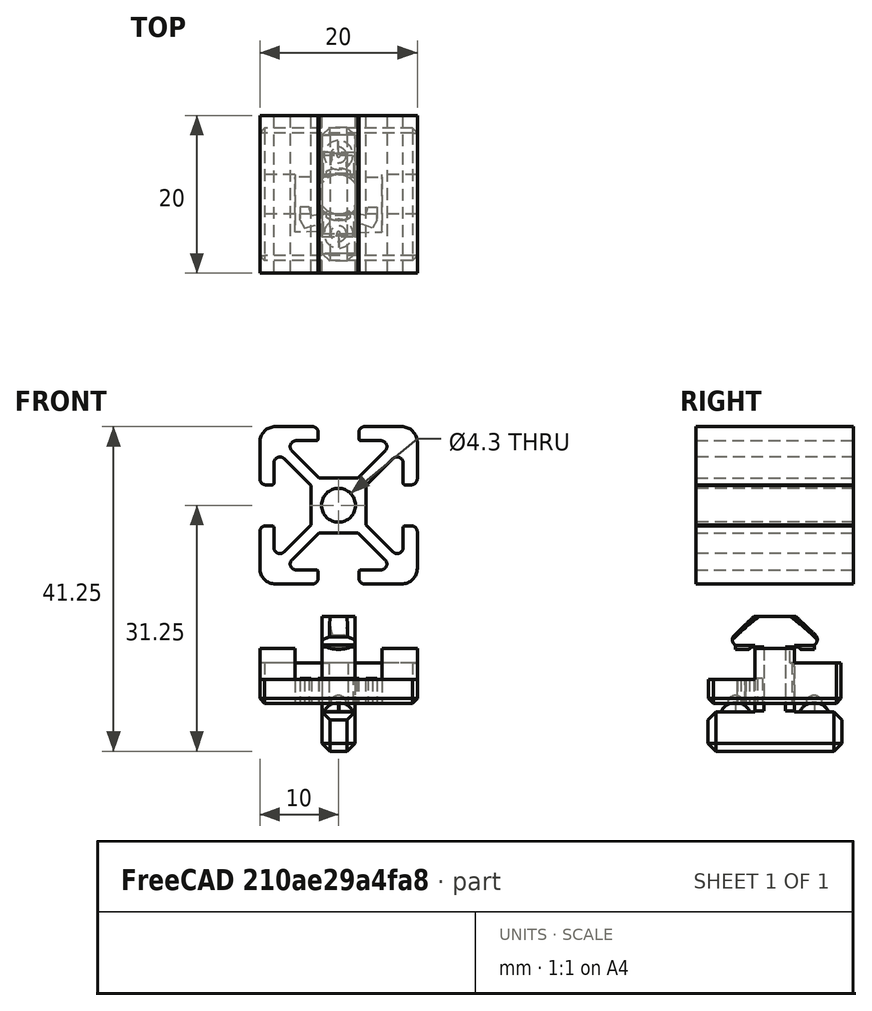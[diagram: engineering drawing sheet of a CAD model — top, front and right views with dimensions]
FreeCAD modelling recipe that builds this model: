
FCSTD DOCUMENT  (FreeCAD 0.18R)
Label: Quickrelease-Parts
License: All rights reserved
LicenseURL: http://en.wikipedia.org/wiki/All_rights_reserved
objects: Sketcher::SketchObject×8, Mesh::Feature×6, PartDesign::Pad×4, PartDesign::Pocket×3, PartDesign::Body×3, PartDesign::PolarPattern×2, PartDesign::Chamfer×2, App::Part×2, PartDesign::SubtractiveSphere×1, PartDesign::Groove×1, PartDesign::AdditiveSphere×1, Part::Compound×1, Spreadsheet::Sheet×1
note: 36 computed .brp shape members not serialized (recipe doc carries the construction recipe); baked Part::Feature solids carry a one-line shape summary decoded from their .brp

FEATURE [Sketcher::SketchObject] Sketch  label="Cutout"
  MapMode = 5
  Support = -> [XY_Plane]
  sketch-geometry (22):
    g0: ArcOfCircle CenterX=0 CenterY=0 CenterZ=0 NormalX=0 NormalY=0 NormalZ=1 AngleXU=0 Radius=2.5 StartAngle=2.64666 EndAngle=3.63653
    g1: ArcOfCircle CenterX=0 CenterY=0 CenterZ=0 NormalX=0 NormalY=0 NormalZ=1 AngleXU=0 Radius=2.5 StartAngle=5.78825 EndAngle=6.77812
    g2: LineSegment StartX=-2.2 StartY=1.18743 StartZ=0 EndX=-2.2 EndY=5.5 EndZ=0
    g3: LineSegment StartX=-2.2 StartY=5.5 StartZ=0 EndX=4.8 EndY=5.5 EndZ=0
    g4: LineSegment StartX=-2.2 StartY=-1.18743 StartZ=0 EndX=-2.2 EndY=-5.5 EndZ=0
    g5: LineSegment StartX=-2.2 StartY=-5.5 StartZ=0 EndX=4.8 EndY=-5.5 EndZ=0
    g6: LineSegment StartX=4.72217 StartY=-2.53995 StartZ=0 EndX=4.8 EndY=-5.5 EndZ=0
    g7: LineSegment StartX=2.2 StartY=-1.18743 StartZ=0 EndX=2.67744 EndY=-3.43203 EndZ=0
    g8: LineSegment StartX=2.67744 StartY=-3.43203 StartZ=0 EndX=1.6 EndY=-3.74347 EndZ=0
    g9: LineSegment StartX=1.6 StartY=-3.74347 StartZ=0 EndX=1.6 EndY=-4.86467 EndZ=0
    g10: LineSegment StartX=1.6 StartY=-4.86467 StartZ=0 EndX=3.24458 EndY=-4.86467 EndZ=0
    g11: LineSegment StartX=3.24458 StartY=-4.86467 StartZ=0 EndX=4.3 EndY=-4.34487 EndZ=0
    g12: LineSegment StartX=4.3 StartY=-4.34487 StartZ=0 EndX=3.77118 EndY=-2.50776 EndZ=0
    g13: LineSegment StartX=2.2 StartY=1.18743 StartZ=0 EndX=2.67744 EndY=3.43203 EndZ=0
    g14: LineSegment StartX=2.67744 StartY=3.43203 StartZ=0 EndX=1.6 EndY=3.74347 EndZ=0
    g15: LineSegment StartX=1.6 StartY=3.74347 StartZ=0 EndX=1.6 EndY=4.86467 EndZ=0
    g16: LineSegment StartX=1.6 StartY=4.86467 StartZ=0 EndX=3.24458 EndY=4.86467 EndZ=0
    g17: LineSegment StartX=3.24458 StartY=4.86467 StartZ=0 EndX=4.3 EndY=4.34487 EndZ=0
    g18: LineSegment StartX=4.3 StartY=4.34487 StartZ=0 EndX=3.65012 EndY=2.51975 EndZ=0
    g19: LineSegment StartX=4.82978 StartY=2.36526 StartZ=0 EndX=4.8 EndY=5.5 EndZ=0
    g20: ArcOfCircle CenterX=4.24748 CenterY=2.5 CenterZ=0 NormalX=0 NormalY=0 NormalZ=1 AngleXU=0 Radius=0.597689 StartAngle=3.10855 EndAngle=6.0558
    g21: ArcOfCircle CenterX=4.24748 CenterY=-2.5 CenterZ=0 NormalX=0 NormalY=0 NormalZ=1 AngleXU=0 Radius=0.476368 StartAngle=6.19922 EndAngle=9.44107
  constraints (48):
    c: Coincident(g0,g1)
    c: Coincident(g0,g-1)
    c: Radius(g0) = 2.5
    c: Coincident(g2,g3)
    c: Coincident(g4,g5)
    c: Coincident(g7,g8)
    c: Coincident(g8,g9)
    c: Coincident(g9,g10)
    c: Coincident(g10,g11)
    c: Coincident(g11,g12)
    c: Coincident(g13,g14)
    c: Coincident(g14,g15)
    c: Coincident(g15,g16)
    c: Coincident(g16,g17)
    c: Coincident(g17,g18)
    c: Coincident(g3,g19)
    c: Coincident(g6,g5)
    c: Coincident(g0,g4)
    c: Coincident(g0,g2)
    c: Coincident(g1,g13)
    c: Coincident(g1,g7)
    c: Vertical(g2)
    c: Horizontal(g3)
    c: Symmetric(g0,g0,g-1)
    c: Vertical(g15)
    c: Symmetric(g13,g7,g-1)
    c: Symmetric(g14,g8,g-1)
    c: Symmetric(g15,g9,g-1)
    c: Horizontal(g16)
    c: Horizontal(g10)
    c: Symmetric(g11,g17,g-1)
    c: Symmetric(g4,g2,g-1)
    c: Coincident(g18,g20)
    c: Coincident(g19,g20)
    c: Coincident(g12,g21)
    c: Coincident(g6,g21)
    c: Symmetric(g20,g21,g-1)
    c: DistanceX(g2,g15) = 3.8
    c: DistanceY(g21,g20) = 5
    c: Symmetric(g5,g3,g-1)
    c: Radius(g1) = 2.5
    c: Vertical(g1,g1)
    c: DistanceX(g0,g1) = 2.2
    c: DistanceY(g4,g2) = 11
    c: DistanceX(g4,g5) = 7
    c: Equal(g16,g10)
    c: DistanceX(g0,g0) = 2.2
    c: DistanceX(g17,g3) = 0.5
FEATURE [Sketcher::SketchObject] Sketch001  label="BodyProfile"
  MapMode = 5
  Placement = pos=(0,0,0) rot=(1,0,0;1.5708rad)
  Support = -> [XZ_Plane]
  expr: Constraints.Clamping Width = Param.thickness + Param.tolerance
  sketch-geometry (9):
    g0: LineSegment StartX=-8.4 StartY=0 StartZ=0 EndX=-8.4 EndY=-5.15 EndZ=0
    g1: LineSegment StartX=-8.4 StartY=-5.15 StartZ=0 EndX=8.4 EndY=-5.15 EndZ=0
    g2: LineSegment StartX=8.4 StartY=-5.15 StartZ=0 EndX=8.4 EndY=-2.15 EndZ=0
    g3: LineSegment StartX=8.4 StartY=-2.15 StartZ=0 EndX=2.5 EndY=-2.15 EndZ=0
    g4: LineSegment StartX=2.5 StartY=-2.15 StartZ=0 EndX=2.5 EndY=0 EndZ=0
    g5: LineSegment StartX=2.5 StartY=0 StartZ=0 EndX=2.5 EndY=1.8 EndZ=0
    g6: LineSegment StartX=2.5 StartY=1.8 StartZ=0 EndX=-2.5 EndY=1.8 EndZ=0
    g7: LineSegment StartX=-2.5 StartY=1.8 StartZ=0 EndX=-2.5 EndY=0 EndZ=0
    g8: LineSegment StartX=-2.5 StartY=0 StartZ=0 EndX=-8.4 EndY=0 EndZ=0
  constraints (25):
    c: Coincident(g2,g3)
    c: Coincident(g3,g4)
    c: Coincident(g4,g5)
    c: Coincident(g5,g6)
    c: Coincident(g6,g7)
    c: Coincident(g7,g8)
    c: Coincident(g0,g8)
    c: Vertical(g0)
    c: Vertical(g2)
    c: Vertical(g4)
    c: Horizontal(g8)
    c: Symmetric(g7,g4,g-2)
    c: Vertical(g5)
    c: Vertical(g7)
    c: DistanceX(g6,g5) = 5
    c: DistanceX(g0,g-1) = 8.4
    c: DistanceY(g7,g6) = 1.8
    c: Horizontal(g6)
    c: Horizontal(g3)
    c: DistanceY(g3,g4) = 2.15  'Clamping Width'
    c: Symmetric(g1,g1,g-2)
    c: PointOnObject(g0,g-1)
    c: DistanceY(g1,g3) = 3
    c: Coincident(g2,g1)
    c: Coincident(g0,g1)
FEATURE [PartDesign::Pad] Pad
  Length = 20
  Length2 = 100
  Midplane = true
  Placement = pos=(0,0,0) rot=(1,0,0;1.5708rad)
  Profile = -> Sketch001
  Type = 0
FEATURE [PartDesign::Pocket] Pocket
  BaseFeature = -> Pad
  Length = 20
  Length2 = 100
  Midplane = true
  Placement = pos=(0,0,0) rot=(1,0,0;1.5708rad)
  Profile = -> Sketch
  Reversed = true
  Type = 0
FEATURE [Sketcher::SketchObject] Sketch009  label="SpringFlat"
  MapMode = 5
  Support = -> [XY_Plane]
  sketch-geometry (4):
    g0: LineSegment StartX=1.17655 StartY=5.27101 StartZ=0 EndX=5.09033 EndY=5.27101 EndZ=0
    g1: LineSegment StartX=5.09033 StartY=5.27101 StartZ=0 EndX=5.09033 EndY=-5.27101 EndZ=0
    g2: LineSegment StartX=5.09033 StartY=-5.27101 StartZ=0 EndX=1.17655 EndY=-5.27101 EndZ=0
    g3: LineSegment StartX=1.17655 StartY=-5.27101 StartZ=0 EndX=1.17655 EndY=5.27101 EndZ=0
  constraints (8):
    c: Coincident(g0,g1)
    c: Coincident(g1,g2)
    c: Coincident(g2,g3)
    c: Coincident(g3,g0)
    c: Horizontal(g0)
    c: Horizontal(g2)
    c: Vertical(g3)
    c: Symmetric(g0,g1,g-1)
FEATURE [PartDesign::Pocket] Pocket001
  BaseFeature = -> Pocket
  Length = 4
  Length2 = 0
  Midplane = true
  Placement = pos=(0,0,0) rot=(1,0,0;1.5708rad)
  Profile = -> Sketch009
  Type = 0
  expr: Length = Param.thickness * 2
FEATURE [PartDesign::SubtractiveSphere] Sphere001
  Angle1 = -90
  Angle2 = 90
  Angle3 = 360
  AttacherType = Attacher::AttachEngine3D
  AttachmentOffset = pos=(5,0,0) rot=(0,0,1;0rad)
  BaseFeature = -> Pocket001
  MapMode = 5
  Placement = pos=(5,-1.1e-15,-5.15) rot=(1,0,0;3.14159rad)
  Radius = 1
  Support = -> [Pocket001]
FEATURE [PartDesign::PolarPattern] PolarPattern002
  Angle = 360
  Axis = -> Z_Axis
  BaseFeature = -> Sphere001
  Occurrences = 2
  Originals = -> [Sphere001]
  Placement = pos=(5,1e-15,-5.15) rot=(1,0,0;3.14159rad)
FEATURE [PartDesign::Chamfer] Chamfer
  Base = -> PolarPattern002 [Edge11,Edge10,Edge9,Edge2,Edge42,Edge36,Edge4,Edge3]
  BaseFeature = -> PolarPattern002
  Placement = pos=(5,1e-15,-5.15) rot=(1,0,0;3.14159rad)
  Size = 0.6
FEATURE [Sketcher::SketchObject] Sketch011
  MapMode = 5
  Support = -> [XY_Plane]
  sketch-geometry (4):
    g0: LineSegment StartX=-2.59862 StartY=-5.51836 StartZ=0 EndX=-1.94057 EndY=-5.51836 EndZ=0
    g1: LineSegment StartX=-1.94057 StartY=-5.51836 StartZ=0 EndX=-1.94057 EndY=5.51836 EndZ=0
    g2: LineSegment StartX=-1.94057 StartY=5.51836 StartZ=0 EndX=-2.59862 EndY=5.51836 EndZ=0
    g3: LineSegment StartX=-2.59862 StartY=5.51836 StartZ=0 EndX=-2.59862 EndY=-5.51836 EndZ=0
  constraints (8):
    c: Coincident(g0,g1)
    c: Coincident(g1,g2)
    c: Coincident(g2,g3)
    c: Coincident(g3,g0)
    c: Horizontal(g0)
    c: Horizontal(g2)
    c: Vertical(g1)
    c: Symmetric(g0,g2,g-1)
FEATURE [PartDesign::Pocket] Pocket002
  BaseFeature = -> Chamfer
  Length = 5
  Length2 = 100
  Placement = pos=(5,1e-15,-5.15) rot=(1,0,0;3.14159rad)
  Profile = -> Sketch011
  Reversed = true
  Type = 0
FEATURE [PartDesign::Body] Body  label="LockBody"
  Group = -> [Sketch,Sketch001,Pad,Pocket,Sketch009,Pocket001,Sphere001,PolarPattern002,Chamfer,Sketch011,Pocket002]
  Origin = -> Origin
  Placement = pos=(0,0,-10) rot=(0,0,-1;1.5708rad)
  Tip = -> Pocket002
FEATURE [Sketcher::SketchObject] Sketch018  label="LockKey-Profile003"
  MapMode = 5
  Placement = pos=(0,0,0) rot=(1,0,0;1.5708rad)
  Support = -> [XZ_Plane010]
  expr: Constraints[23] = Param.thickness + 4.0999999999999996 + Param.tolerance
  sketch-geometry (14):
    g0: LineSegment StartX=-2.5 StartY=2.2 StartZ=0 EndX=-4.9399 EndY=2.2 EndZ=0
    g1: LineSegment StartX=-5.19157 StartY=3.4796 StartZ=0 EndX=-2.66572 EndY=5.8764 EndZ=0
    g2: LineSegment StartX=-2.66572 StartY=5.8764 StartZ=0 EndX=2.66572 EndY=5.8764 EndZ=0
    g3: LineSegment StartX=2.66572 StartY=5.8764 StartZ=0 EndX=5.31297 EndY=3.29057 EndZ=0
    g4: LineSegment StartX=-2.5 StartY=2.2 StartZ=0 EndX=-2.5 EndY=-6.25 EndZ=0
    g5: LineSegment StartX=-2.5 StartY=-6.25 StartZ=0 EndX=-8.5 EndY=-6.25 EndZ=0
    g6: LineSegment StartX=-8.5 StartY=-6.25 StartZ=0 EndX=-8.5 EndY=-11.25 EndZ=0
    g7: LineSegment StartX=-8.5 StartY=-11.25 StartZ=0 EndX=8.5 EndY=-11.25 EndZ=0
    g8: LineSegment StartX=8.5 StartY=-11.25 StartZ=0 EndX=8.5 EndY=-6.25 EndZ=0
    g9: LineSegment StartX=8.5 StartY=-6.25 StartZ=0 EndX=2.5 EndY=-6.25 EndZ=0
    g10: LineSegment StartX=2.5 StartY=-6.25 StartZ=0 EndX=2.5 EndY=2.2 EndZ=0
    g11: LineSegment StartX=2.5 StartY=2.2 StartZ=0 EndX=4.9399 EndY=2.2 EndZ=0
    g12: ArcOfCircle CenterX=-4.55856 CenterY=2.93955 CenterZ=0 NormalX=0 NormalY=0 NormalZ=1 AngleXU=0 Radius=0.832074 StartAngle=2.43527 EndAngle=4.23632
    g13: ArcOfCircle CenterX=4.55856 CenterY=2.93955 CenterZ=0 NormalX=0 NormalY=0 NormalZ=1 AngleXU=0 Radius=0.832074 StartAngle=5.18846 EndAngle=6.71868
  constraints (33):
    c: Coincident(g1,g2)
    c: Coincident(g2,g3)
    c: Coincident(g4,g5)
    c: Coincident(g9,g10)
    c: Coincident(g10,g11)
    c: Horizontal(g0)
    c: Horizontal(g11)
    c: Horizontal(g9)
    c: Horizontal(g5)
    c: Vertical(g6)
    c: Vertical(g8)
    c: Coincident(g13,g3)
    c: Coincident(g13,g11)
    c: Coincident(g12,g1)
    c: Coincident(g12,g0)
    c: Symmetric(g13,g12,g-2)
    c: Equal(g13,g12)
    c: Symmetric(g1,g2,g-2)
    c: Coincident(g0,g4)
    c: Symmetric(g0,g10,g-2)
    c: DistanceX(g0,g10) = 5
    c: Vertical(g4)
    c: Symmetric(g7,g7,g-2)
    c: DistanceY(g4,g-1) = 6.25
    c: DistanceY(g-1,g0) = 2.2
    c: DistanceX(g6,g8) = 17
    c: Equal(g5,g9)
    c: DistanceY(g7,g9) = 5
    c: Coincident(g6,g7)
    c: Coincident(g7,g8)
    c: Coincident(g6,g5)
    c: Coincident(g9,g8)
    c: Equal(g4,g10)
FEATURE [PartDesign::Pad] Pad009
  Length = 4.2
  Length2 = 100
  Midplane = true
  Placement = pos=(0,0,0) rot=(1,0,0;1.5708rad)
  Profile = -> Sketch018
  Type = 0
FEATURE [Sketcher::SketchObject] Sketch019  label="ISP5-Shape003"
  MapMode = 5
  Placement = pos=(0,0,0) rot=(1,0,0;1.5708rad)
  expr: Constraints[29] = 4 + Param.thickness + Param.tolerance
  sketch-geometry (11):
    g0: LineSegment StartX=0 StartY=6.35 StartZ=0 EndX=2.4 EndY=6.35 EndZ=0
    g1: LineSegment StartX=2.4 StartY=6.35 StartZ=0 EndX=5.75 EndY=2.96706 EndZ=0
    g2: LineSegment StartX=5.75 StartY=2.96706 StartZ=0 EndX=5.75 EndY=1.6 EndZ=0
    g3: LineSegment StartX=5.75 StartY=1.6 StartZ=0 EndX=3.3 EndY=1.6 EndZ=0
    g4: LineSegment StartX=2.5 StartY=2 StartZ=0 EndX=2.5 EndY=-6.15 EndZ=0
    g5: LineSegment StartX=2.5 StartY=-6.15 StartZ=0 EndX=6.85109 EndY=-6.15 EndZ=0
    g6: LineSegment StartX=6.85109 StartY=-6.15 StartZ=0 EndX=6.85109 EndY=7.66399 EndZ=0
    g7: LineSegment StartX=6.85109 StartY=7.66399 StartZ=0 EndX=0 EndY=7.66399 EndZ=0
    g8: LineSegment StartX=0 StartY=7.66399 StartZ=0 EndX=0 EndY=6.35 EndZ=0
    g9: LineSegment StartX=2.5 StartY=2 StartZ=0 EndX=3.3 EndY=2 EndZ=0
    g10: LineSegment StartX=3.3 StartY=2 StartZ=0 EndX=3.3 EndY=1.6 EndZ=0
  constraints (30):
    c: Coincident(g0,g1)
    c: Coincident(g1,g2)
    c: Coincident(g2,g3)
    c: Coincident(g4,g5)
    c: Vertical(g4)
    c: Horizontal(g0)
    c: Horizontal(g5)
    c: Horizontal(g3)
    c: Coincident(g7,g8)
    c: Coincident(g8,g0)
    c: Coincident(g6,g7)
    c: Coincident(g5,g6)
    c: Vertical(g6)
    c: Horizontal(g7)
    c: Vertical(g8)
    c: PointOnObject(g0,g-2)
    c: DistanceY(g-1,g3) = 1.6
    c: DistanceX(g-1,g2) = 5.75
    c: Vertical(g2)
    c: DistanceY(g-1,g0) = 6.35
    c: DistanceX(g0,g0) = 2.4
    c: Coincident(g9,g10)
    c: Coincident(g10,g3)
    c: Coincident(g4,g9)
    c: Horizontal(g9)
    c: Vertical(g10)
    c: DistanceY(g-1,g4) = 2
    c: DistanceX(g-1,g4) = 2.5
    c: DistanceX(g9,g9) = 0.8
    c: DistanceY(g4,g-1) = 6.15
FEATURE [Sketcher::SketchObject] Sketch020
  MapMode = 5
  Placement = pos=(0,0,0) rot=(0.57735,0.57735,0.57735;2.0944rad)
  Support = -> [YZ_Plane010]
  sketch-geometry (3):
    g0: ArcOfCircle CenterX=-2e-16 CenterY=5.7 CenterZ=0 NormalX=0 NormalY=0 NormalZ=1 AngleXU=0 Radius=4 StartAngle=4.15967 EndAngle=5.2651
    g1: LineSegment [constr] StartX=0 StartY=0 StartZ=0 EndX=0 EndY=1.7 EndZ=0
    g2: LineSegment StartX=-2.1 StartY=2.29559 StartZ=0 EndX=2.1 EndY=2.29559 EndZ=0
  constraints (9):
    c: Symmetric(g0,g0,g-2)
    c: DistanceX(g0,g0) = 4.2
    c: PointOnObject(g1,g0)
    c: Vertical(g1)
    c: Coincident(g-1,g1)
    c: DistanceY(g1,g1) = 1.7
    c: Radius(g0) = 4
    c: Coincident(g2,g0)
    c: Coincident(g2,g0)
FEATURE [PartDesign::Pad] Pad010
  BaseFeature = -> Pad009
  Length = 10
  Length2 = 100
  Midplane = true
  Placement = pos=(0,0,0) rot=(1,0,0;1.5708rad)
  Profile = -> Sketch020
  Type = 0
FEATURE [PartDesign::Groove] Groove003
  Angle = 360
  Axis = (0,2e-16,1)
  Base = (0,0,0)
  BaseFeature = -> Pad010
  Placement = pos=(0,0,0) rot=(1,0,0;1.5708rad)
  Profile = -> Sketch019
  ReferenceAxis = -> Sketch019 [V_Axis]
FEATURE [PartDesign::AdditiveSphere] Sphere004
  Angle1 = -83
  Angle2 = 90
  Angle3 = 358
  AttacherType = Attacher::AttachEngine3D
  AttachmentOffset = pos=(5,0,-4.2) rot=(0,0,-1;0.017453rad)
  BaseFeature = -> Groove003
  MapMode = 5
  Placement = pos=(5,-1.6e-15,-7.05) rot=(0.999962,0.008727,0;3.14159rad)
  Radius = 2
  Support = -> [Groove003]
FEATURE [PartDesign::PolarPattern] PolarPattern005
  Angle = 360
  Axis = -> Z_Axis010
  BaseFeature = -> Sphere004
  Occurrences = 2
  Originals = -> [Sphere004]
  Placement = pos=(5,2e-15,-7.05) rot=(0.999962,0.008727,0;3.14159rad)
FEATURE [PartDesign::Chamfer] Chamfer004
  Base = -> PolarPattern005 [Face11,Face10,Face12]
  BaseFeature = -> PolarPattern005
  Placement = pos=(5,2e-15,-7.05) rot=(0.999962,0.008727,0;3.14159rad)
  Size = 1
FEATURE [PartDesign::Body] Body007  label="LockKey"
  Group = -> [Pad009,Pad010,Sketch018,Sketch019,Groove003,Sphere004,Sketch020,PolarPattern005,Chamfer004]
  Origin = -> Origin010
  Placement = pos=(0,0,-10) rot=(0,0,-1;1.5708rad)
  Tip = -> Chamfer004
FEATURE [Part::Compound] Compound  label="Key-Body-Combo"
  Links = -> [Body,Body007]
FEATURE [Spreadsheet::Sheet] Spreadsheet  label="Param"
  cells = A1=Sheet Thickness; B1(thickness)=2; C1=The specified thickness of the sheet to clamp.; A2=Sheet Thickness Tolerance; B2(tolerance)=0.14999999999999999; C2=Adds to the sheet thickness and results in the distance between the surface of the extrusion profile and the bottom side of the clamp.
FEATURE [App::Part] Part  label="Key-Clamp-Combo"
  Group = -> [Body,Body007,Compound,Spreadsheet]
  Origin = -> Origin011
FEATURE [Mesh::Feature] Mesh007  label="LockBody-4mm (Meshed)"
  Placement = pos=(0,18,-33) rot=(0,0,1;0rad)
FEATURE [Mesh::Feature] Mesh008  label="LockKey-4mm (Meshed)"
  Placement = pos=(-7.8e-15,57,-3) rot=(0,1,0;1.5708rad)
FEATURE [Mesh::Feature] Mesh009  label="LockKey-3mm (Meshed)001"
  Placement = pos=(-32,0,-7.1e-15) rot=(0,1,0;1.5708rad)
FEATURE [Mesh::Feature] Mesh010  label="LockBody-3mm (Meshed)"
FEATURE [Mesh::Feature] Mesh  label="LockKey-2mm (Meshed)"
  Placement = pos=(0,48,0) rot=(0,1,0;1.5708rad)
FEATURE [Mesh::Feature] Mesh011  label="LockBody-2mm (Meshed)"
FEATURE [App::Part] Part001  label="MeshedParts"
  Group = -> [Mesh007,Mesh008,Mesh009,Mesh010,Mesh,Mesh011]
  Origin = -> Origin012
FEATURE [Sketcher::SketchObject] CopySketch030  label="ISP5-L20-Profile001"
  MapMode = 5
  sketch-geometry (70):
    g0: LineSegment StartX=-2.5 StartY=3.5 StartZ=0 EndX=-5.91967 EndY=6.91967 EndZ=0
    g1: LineSegment StartX=-5.38934 StartY=8.2 StartZ=0 EndX=-2.85 EndY=8.2 EndZ=0
    g2: LineSegment StartX=-3.35 StartY=10 StartZ=0 EndX=-8 EndY=10 EndZ=0
    g3: LineSegment StartX=-10 StartY=8 StartZ=0 EndX=-10 EndY=3.35 EndZ=0
    g4: LineSegment StartX=-9.25 StartY=2.6 StartZ=0 EndX=-8.45 EndY=2.6 EndZ=0
    g5: LineSegment StartX=-8.2 StartY=2.85 StartZ=0 EndX=-8.2 EndY=5.38934 EndZ=0
    g6: LineSegment StartX=-6.91967 StartY=5.91967 StartZ=0 EndX=-3.5 EndY=2.5 EndZ=0
    g7: LineSegment StartX=-2.6 StartY=9.25 StartZ=0 EndX=-2.6 EndY=8.45 EndZ=0
    g8: ArcOfCircle CenterX=-8 CenterY=8 CenterZ=0 NormalX=0 NormalY=0 NormalZ=1 AngleXU=0 Radius=2 StartAngle=1.5708 EndAngle=3.14159
    g9: ArcOfCircle CenterX=-3.35 CenterY=9.25 CenterZ=0 NormalX=0 NormalY=0 NormalZ=1 AngleXU=0 Radius=0.75 StartAngle=6e-16 EndAngle=1.5708
    g10: ArcOfCircle CenterX=-9.25 CenterY=3.35 CenterZ=0 NormalX=0 NormalY=0 NormalZ=1 AngleXU=0 Radius=0.75 StartAngle=3.14159 EndAngle=4.71239
    g11: ArcOfCircle CenterX=-5.38934 CenterY=7.45 CenterZ=0 NormalX=0 NormalY=0 NormalZ=1 AngleXU=0 Radius=0.75 StartAngle=1.5708 EndAngle=3.92699
    g12: ArcOfCircle CenterX=-7.45 CenterY=5.38934 CenterZ=0 NormalX=0 NormalY=0 NormalZ=1 AngleXU=0 Radius=0.75 StartAngle=0.785398 EndAngle=3.14159
    g13: LineSegment [constr] StartX=-5.38934 StartY=7.45 StartZ=0 EndX=-7.45 EndY=5.38934 EndZ=0
    g14: ArcOfCircle CenterX=-2.85 CenterY=8.45 CenterZ=0 NormalX=0 NormalY=0 NormalZ=1 AngleXU=0 Radius=0.25 StartAngle=4.71239 EndAngle=6.28319
    g15: Circle CenterX=0 CenterY=0 CenterZ=0 NormalX=0 NormalY=0 NormalZ=1 AngleXU=0 Radius=2.15
    g16: LineSegment StartX=2.5 StartY=3.5 StartZ=0 EndX=5.91967 EndY=6.91967 EndZ=0
    g17: LineSegment StartX=3.5 StartY=-2.5 StartZ=0 EndX=6.91967 EndY=-5.91967 EndZ=0
    g18: LineSegment StartX=2.5 StartY=-3.5 StartZ=0 EndX=5.91967 EndY=-6.91967 EndZ=0
    g19: LineSegment StartX=-2.5 StartY=-3.5 StartZ=0 EndX=-5.91967 EndY=-6.91967 EndZ=0
    g20: LineSegment StartX=-3.5 StartY=-2.5 StartZ=0 EndX=-6.91967 EndY=-5.91967 EndZ=0
    g21: LineSegment StartX=3.5 StartY=2.5 StartZ=0 EndX=6.91967 EndY=5.91967 EndZ=0
    g22: ArcOfCircle CenterX=-7.45 CenterY=-5.38934 CenterZ=0 NormalX=0 NormalY=0 NormalZ=1 AngleXU=0 Radius=0.75 StartAngle=3.14159 EndAngle=5.49779
    g23: ArcOfCircle CenterX=-5.38934 CenterY=-7.45 CenterZ=0 NormalX=0 NormalY=0 NormalZ=1 AngleXU=0 Radius=0.75 StartAngle=2.35619 EndAngle=4.71239
    g24: ArcOfCircle CenterX=5.38934 CenterY=-7.45 CenterZ=0 NormalX=0 NormalY=0 NormalZ=1 AngleXU=0 Radius=0.75 StartAngle=4.71239 EndAngle=7.06858
    g25: ArcOfCircle CenterX=7.45 CenterY=-5.38934 CenterZ=0 NormalX=0 NormalY=0 NormalZ=1 AngleXU=0 Radius=0.75 StartAngle=3.92699 EndAngle=6.28319
    g26: ArcOfCircle CenterX=5.38934 CenterY=7.45 CenterZ=0 NormalX=0 NormalY=0 NormalZ=1 AngleXU=0 Radius=0.75 StartAngle=5.49779 EndAngle=7.85398
    g27: ArcOfCircle CenterX=7.45 CenterY=5.38934 CenterZ=0 NormalX=0 NormalY=0 NormalZ=1 AngleXU=0 Radius=0.75 StartAngle=6e-16 EndAngle=2.35619
    g28: LineSegment StartX=-5.38934 StartY=-8.2 StartZ=0 EndX=-2.85 EndY=-8.2 EndZ=0
    g29: LineSegment StartX=2.85 StartY=-8.2 StartZ=0 EndX=5.38934 EndY=-8.2 EndZ=0
    g30: LineSegment StartX=8.2 StartY=-5.38934 StartZ=0 EndX=8.2 EndY=-2.85 EndZ=0
    g31: LineSegment StartX=8.2 StartY=5.38934 StartZ=0 EndX=8.2 EndY=2.85 EndZ=0
    g32: LineSegment StartX=5.38934 StartY=8.2 StartZ=0 EndX=2.85 EndY=8.2 EndZ=0
    g33: LineSegment StartX=-8.2 StartY=-5.38934 StartZ=0 EndX=-8.2 EndY=-2.85 EndZ=0
    g34: ArcOfCircle CenterX=-8.45 CenterY=-2.85 CenterZ=0 NormalX=0 NormalY=0 NormalZ=1 AngleXU=0 Radius=0.25 StartAngle=7e-16 EndAngle=1.5708
    g35: ArcOfCircle CenterX=-2.85 CenterY=-8.45 CenterZ=0 NormalX=0 NormalY=0 NormalZ=1 AngleXU=0 Radius=0.25 StartAngle=1e-15 EndAngle=1.5708
    g36: ArcOfCircle CenterX=2.85 CenterY=-8.45 CenterZ=0 NormalX=0 NormalY=0 NormalZ=1 AngleXU=0 Radius=0.25 StartAngle=1.5708 EndAngle=3.14159
    g37: ArcOfCircle CenterX=8.45 CenterY=-2.85 CenterZ=0 NormalX=0 NormalY=0 NormalZ=1 AngleXU=0 Radius=0.25 StartAngle=1.5708 EndAngle=3.14159
    g38: LineSegment StartX=2.6 StartY=9.25 StartZ=0 EndX=2.6 EndY=8.45 EndZ=0
    g39: LineSegment StartX=8.45 StartY=2.6 StartZ=0 EndX=9.25 EndY=2.6 EndZ=0
    g40: LineSegment StartX=8.45 StartY=-2.6 StartZ=0 EndX=9.25 EndY=-2.6 EndZ=0
    g41: LineSegment StartX=-8.45 StartY=-2.6 StartZ=0 EndX=-9.25 EndY=-2.6 EndZ=0
    g42: LineSegment StartX=-2.6 StartY=-8.45 StartZ=0 EndX=-2.6 EndY=-9.25 EndZ=0
    g43: LineSegment StartX=2.6 StartY=-8.45 StartZ=0 EndX=2.6 EndY=-9.25 EndZ=0
    g44: ArcOfCircle CenterX=8.45 CenterY=2.85 CenterZ=0 NormalX=0 NormalY=0 NormalZ=1 AngleXU=0 Radius=0.25 StartAngle=3.14159 EndAngle=4.71239
    g45: LineSegment StartX=3.35 StartY=10 StartZ=0 EndX=8 EndY=10 EndZ=0
    g46: ArcOfCircle CenterX=8 CenterY=8 CenterZ=0 NormalX=0 NormalY=0 NormalZ=1 AngleXU=0 Radius=2 StartAngle=2e-16 EndAngle=1.5708
    g47: LineSegment StartX=10 StartY=8 StartZ=0 EndX=10 EndY=3.35 EndZ=0
    g48: ArcOfCircle CenterX=9.25 CenterY=3.35 CenterZ=0 NormalX=0 NormalY=0 NormalZ=1 AngleXU=0 Radius=0.75 StartAngle=4.71239 EndAngle=6.28319
    g49: LineSegment StartX=3.35 StartY=-10 StartZ=0 EndX=8 EndY=-10 EndZ=0
    g50: ArcOfCircle CenterX=8 CenterY=-8 CenterZ=0 NormalX=0 NormalY=0 NormalZ=1 AngleXU=0 Radius=2 StartAngle=4.71239 EndAngle=6.28319
    g51: LineSegment StartX=10 StartY=-8 StartZ=0 EndX=10 EndY=-3.35 EndZ=0
    g52: ArcOfCircle CenterX=9.25 CenterY=-3.35 CenterZ=0 NormalX=0 NormalY=0 NormalZ=1 AngleXU=0 Radius=0.75 StartAngle=1e-16 EndAngle=1.5708
    g53: LineSegment StartX=-3.35 StartY=-10 StartZ=0 EndX=-8 EndY=-10 EndZ=0
    g54: LineSegment StartX=-10 StartY=-8 StartZ=0 EndX=-10 EndY=-3.35 EndZ=0
    g55: ArcOfCircle CenterX=-9.25 CenterY=-3.35 CenterZ=0 NormalX=0 NormalY=0 NormalZ=1 AngleXU=0 Radius=0.75 StartAngle=1.5708 EndAngle=3.14159
    g56: ArcOfCircle CenterX=-3.35 CenterY=-9.25 CenterZ=0 NormalX=0 NormalY=0 NormalZ=1 AngleXU=0 Radius=0.75 StartAngle=4.71239 EndAngle=6.28319
    g57: ArcOfCircle CenterX=3.35 CenterY=-9.25 CenterZ=0 NormalX=0 NormalY=0 NormalZ=1 AngleXU=0 Radius=0.75 StartAngle=3.14159 EndAngle=4.71239
    g58: ArcOfCircle CenterX=3.35 CenterY=9.25 CenterZ=0 NormalX=0 NormalY=0 NormalZ=1 AngleXU=0 Radius=0.75 StartAngle=1.5708 EndAngle=3.14159
    g59: ArcOfCircle CenterX=-8 CenterY=-8 CenterZ=0 NormalX=0 NormalY=0 NormalZ=1 AngleXU=0 Radius=2 StartAngle=3.14159 EndAngle=4.71239
    g60: ArcOfCircle CenterX=-8.45 CenterY=2.85 CenterZ=0 NormalX=0 NormalY=0 NormalZ=1 AngleXU=0 Radius=0.25 StartAngle=4.71239 EndAngle=6.28319
    g61: ArcOfCircle CenterX=2.85 CenterY=8.45 CenterZ=0 NormalX=0 NormalY=0 NormalZ=1 AngleXU=0 Radius=0.25 StartAngle=3.14159 EndAngle=4.71239
    g62: LineSegment StartX=0 StartY=3.5 StartZ=0 EndX=2.5 EndY=3.5 EndZ=0
    g63: LineSegment StartX=0 StartY=3.5 StartZ=0 EndX=-2.5 EndY=3.5 EndZ=0
    g64: LineSegment StartX=-3.5 StartY=2.5 StartZ=0 EndX=-3.5 EndY=0 EndZ=0
    g65: LineSegment StartX=-3.5 StartY=0 StartZ=0 EndX=-3.5 EndY=-2.5 EndZ=0
    g66: LineSegment StartX=-2.5 StartY=-3.5 StartZ=0 EndX=0 EndY=-3.5 EndZ=0
    g67: LineSegment StartX=0 StartY=-3.5 StartZ=0 EndX=2.5 EndY=-3.5 EndZ=0
    g68: LineSegment StartX=3.5 StartY=-2.5 StartZ=0 EndX=3.5 EndY=0 EndZ=0
    g69: LineSegment StartX=3.5 StartY=0 StartZ=0 EndX=3.5 EndY=2.5 EndZ=0
  constraints (173):
    c: Vertical(g7)
    c: Horizontal(g1)
    c: Vertical(g5)
    c: Horizontal(g4)
    c: Coincident(g2,g9)
    c: Coincident(g9,g7)
    c: Radius(g9) = 0.75
    c: DistanceY(g1,g2) = 1.8
    c: Coincident(g3,g10)
    c: Coincident(g10,g4)
    c: Radius(g10) = 0.75
    c: Horizontal(g9,g7)
    c: Vertical(g2,g9)
    c: Coincident(g0,g11)
    c: Coincident(g11,g1)
    c: Vertical(g1,g11)
    c: Radius(g11) = 0.75
    c: Coincident(g12,g6)
    c: Coincident(g12,g5)
    c: Equal(g11,g12)
    c: Horizontal(g5,g12)
    c: Coincident(g12,g13)
    c: Coincident(g11,g13)
    c: PointOnObject(g0,g13)
    c: PointOnObject(g6,g13)
    c: Horizontal(g3,g10)
    c: Vertical(g10,g4)
    c: Horizontal(g2)
    c: Vertical(g3)
    c: Parallel(g6,g0)
    c: Tangent(g2,g8) = -1.5708
    c: Tangent(g3,g8) = -1.5708
    c: Radius(g8) = 2
    c: Perpendicular(g13,g6)
    c: Coincident(g7,g14)
    c: Coincident(g1,g14)
    c: Vertical(g14,g1)
    c: Horizontal(g14,g7)
    c: Radius(g14) = 0.25
    c: DistanceX(g3,g5) = 1.8
    c: Coincident(g15,g-1)
    c: Radius(g15) = 2.15
    c: DistanceX(g0,g16) = 5
    c: Symmetric(g16,g0,g-2)
    c: Symmetric(g21,g6,g-2)
    c: Equal(g16,g21)
    c: Parallel(g20,g19)
    c: Parallel(g18,g17)
    c: Symmetric(g6,g20,g-1)
    c: Symmetric(g0,g19,g-1)
    c: Tangent(g16,g26) = -1.5708
    c: Tangent(g21,g27) = 1.5708
    c: Tangent(g17,g25) = -1.5708
    c: Tangent(g18,g24) = 1.5708
    c: Tangent(g19,g23) = -1.5708
    c: Tangent(g20,g22) = 1.5708
    c: Horizontal(g28)
    c: Tangent(g26,g32) = -1.5708
    c: Tangent(g27,g31) = 1.5708
    c: Tangent(g25,g30) = -1.5708
    c: Tangent(g24,g29) = -1.5708
    c: Tangent(g23,g28) = -1.5708
    c: Tangent(g22,g33) = 1.5708
    c: Tangent(g30,g37) = 1.5708
    c: Tangent(g36,g29) = 1.5708
    c: Tangent(g28,g35) = 1.5708
    c: Tangent(g34,g33) = -1.5708
    c: Symmetric(g0,g16,g-2)
    c: Symmetric(g21,g17,g-1)
    c: Symmetric(g18,g19,g-2)
    c: Symmetric(g6,g20,g-1)
    c: Symmetric(g23,g1,g-1)
    c: Symmetric(g24,g26,g-1)
    c: DistanceX(g6,g21) = 7
    c: Vertical(g42)
    c: Vertical(g43)
    c: Tangent(g44,g31) = -1.5708
    c: Tangent(g44,g39) = -1.5708
    c: Tangent(g37,g40) = 1.5708
    c: Tangent(g36,g43) = -1.5708
    c: Tangent(g35,g42) = 1.5708
    c: Tangent(g41,g34) = -1.5708
    c: Symmetric(g5,g27,g-2)
    c: Symmetric(g22,g25,g-2)
    c: Vertical(g7,g35)
    c: Symmetric(g4,g41,g-1)
    c: Symmetric(g7,g38,g-2)
    c: Symmetric(g39,g40,g-1)
    c: Tangent(g45,g46) = 1.5708
    c: Tangent(g46,g47) = 1.5708
    c: Tangent(g47,g48) = 1.5708
    c: Tangent(g49,g50) = -1.5708
    c: Tangent(g50,g51) = -1.5708
    c: Tangent(g51,g52) = -1.5708
    c: Tangent(g54,g55) = 1.5708
    c: Tangent(g55,g41) = -1.5708
    c: Tangent(g40,g52) = 1.5708
    c: Tangent(g48,g39) = -1.5708
    c: Vertical(g51)
    c: Vertical(g47)
    c: Horizontal(g45)
    c: Horizontal(g49)
    c: Horizontal(g53)
    c: Tangent(g45,g58) = 1.5708
    c: Tangent(g38,g58) = -1.5708
    c: Tangent(g43,g57) = -1.5708
    c: Tangent(g49,g57) = -1.5708
    c: Tangent(g53,g56) = 1.5708
    c: Tangent(g42,g56) = 1.5708
    c: DistanceX(g3,g46) = 20
    c: Tangent(g54,g59) = 1.5708
    c: Tangent(g53,g59) = 1.5708
    c: DistanceY(g53,g2) = 20
    c: Symmetric(g54,g51,g-2)
    c: Vertical(g51,g47)
    c: Horizontal(g39)
    c: Horizontal(g40)
    c: Vertical(g54)
    c: DistanceX(g7,g38) = 5.2
    c: DistanceY(g41,g4) = 5.2
    c: DistanceY(g40,g39) = 5.2
    c: Horizontal(g2,g45)
    c: Vertical(g3,g54)
    c: Horizontal(g53,g49)
    c: Vertical(g38)
    c: Horizontal(g32)
    c: Vertical(g30)
    c: Vertical(g31)
    c: Vertical(g33)
    c: Vertical(g5,g33)
    c: Horizontal(g41)
    c: Radius(g46) = 2
    c: Radius(g50) = 2
    c: Radius(g59) = 2
    c: Radius(g56) = 0.75
    c: Symmetric(g42,g43,g-2)
    c: Radius(g35) = 0.25
    c: Radius(g44) = 0.25
    c: Radius(g34) = 0.25
    c: Radius(g37) = 0.25
    c: Tangent(g5,g60) = -1.5708
    c: Tangent(g4,g60) = -1.5708
    c: Radius(g60) = 0.25
    c: Tangent(g61,g38) = -1.5708
    c: Tangent(g32,g61) = 1.5708
    c: Radius(g61) = 0.25
    c: Radius(g36) = 0.25
    c: Horizontal(g1,g32)
    c: Coincident(g62,g63)
    c: Horizontal(g63)
    c: PointOnObject(g62,g-2)
    c: Coincident(g16,g62)
    c: Coincident(g0,g63)
    c: Coincident(g68,g69)
    c: Coincident(g66,g67)
    c: Coincident(g64,g65)
    c: Coincident(g20,g65)
    c: Coincident(g19,g66)
    c: Coincident(g18,g67)
    c: Coincident(g17,g68)
    c: Coincident(g21,g69)
    c: Coincident(g6,g64)
    c: PointOnObject(g64,g-1)
    c: PointOnObject(g68,g-1)
    c: PointOnObject(g66,g-2)
    c: Vertical(g64)
    c: Horizontal(g66)
    c: Horizontal(g67)
    c: Vertical(g69)
    c: Vertical(g68)
    c: DistanceY(g20,g6) = 5
    c: DistanceY(g19,g0) = 7
    c: Vertical(g16,g18)
FEATURE [PartDesign::Pad] Pad011
  Length = 20
  Length2 = 100
  Profile = -> CopySketch030
  Type = 0
FEATURE [PartDesign::Body] Body008  label="ISP5-L20"
  Group = -> [CopySketch030,Pad011]
  Origin = -> Origin013
  Placement = pos=(0,-10,10) rot=(1,0,0;4.71239rad)
  Tip = -> Pad011
